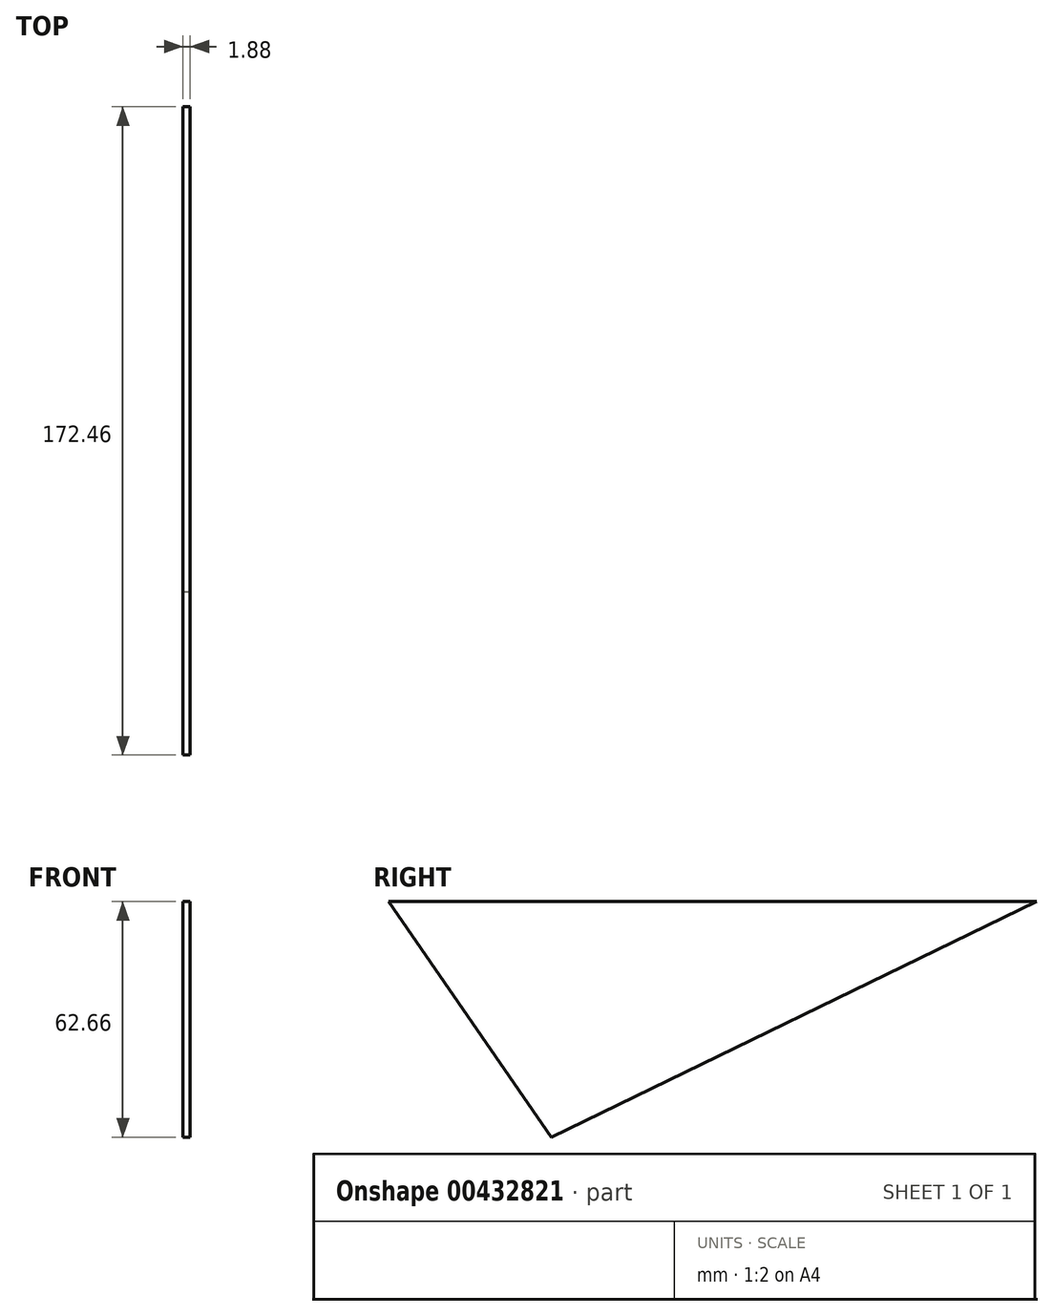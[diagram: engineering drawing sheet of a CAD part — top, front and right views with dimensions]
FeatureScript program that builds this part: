
annotation { "Feature Type Name" : "Feature", "Feature Type Description" : "" }
export const myFeature = defineFeature(function(context is Context, id is Id, definition is map)
    precondition{}
    {
        {
            var Q0;
            Q0=qCreatedBy(makeId("Right.planeOp"),FACE);
            var sketch = newSketch(context, id + "F0", { "sketchPlane" : qUnion([Q0])});
            skLineSegment(sketch, "E0", {"start": v(84.2, 0) * mm, "end": v(-88.26, 0) * mm});
            skLineSegment(sketch, "E1", {"start": v(-88.26, 0) * mm, "end": v(-44.9, -62.66) * mm});
            skLineSegment(sketch, "E2", {"start": v(-44.9, -62.66) * mm, "end": v(84.2, 0) * mm});
            skSolve(sketch);
        }
        {
            var Q0;
            Q0 = qSketchRegion(id + "F0", true);
            extrude(context, id + "F1", {"entities" : qUnion([Q0]), "depth" : 1.88 * mm});
        }
    });
